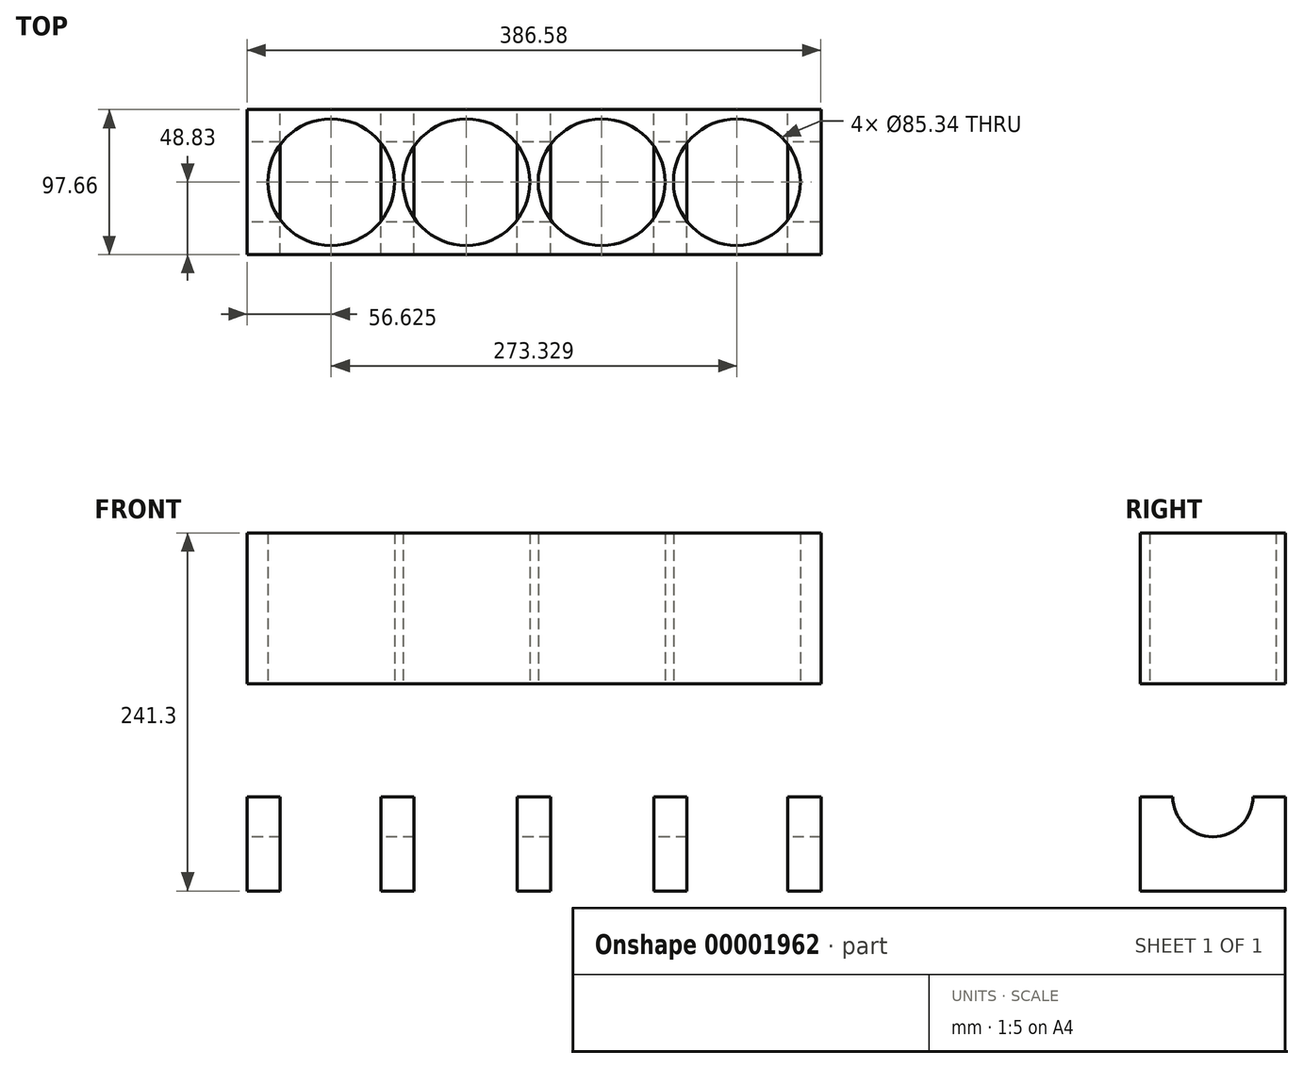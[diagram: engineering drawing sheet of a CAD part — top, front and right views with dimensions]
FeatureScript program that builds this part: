
annotation { "Feature Type Name" : "Feature", "Feature Type Description" : "" }
export const myFeature = defineFeature(function(context is Context, id is Id, definition is map)
    precondition{}
    {
        {
            var Q0;
            Q0=qCreatedBy(makeId("Front.planeOp"),FACE);
            var sketch = newSketch(context, id + "F0", { "sketchPlane" : qUnion([Q0])});
            skLineSegment(sketch, "E0.bottom", {"start": v(-193.3, 0) * mm, "end": v(-170.94, 0) * mm});
            skLineSegment(sketch, "E0.top", {"start": v(-193.3, -63.5) * mm, "end": v(-170.94, -63.5) * mm});
            skLineSegment(sketch, "E0.left", {"start": v(-193.3, 0) * mm, "end": v(-193.3, -63.5) * mm});
            skLineSegment(sketch, "E0.right", {"start": v(193.3, 0) * mm, "end": v(193.3, -63.5) * mm});
            skLineSegment(sketch, "E1", {"start": v(-170.94, 0) * mm, "end": v(-170.94, -63.5) * mm});
            skLineSegment(sketch, "E2", {"start": v(-103.05, 0) * mm, "end": v(-103.05, -63.5) * mm});
            skLineSegment(sketch, "E3", {"start": v(-80.7, 0) * mm, "end": v(-80.7, -63.5) * mm});
            skLineSegment(sketch, "E4", {"start": v(-11.18, 0) * mm, "end": v(-11.18, -63.5) * mm});
            skLineSegment(sketch, "E5", {"start": v(0, 0) * mm, "end": v(0, -63.5) * mm, "construction": true});
            skLineSegment(sketch, "E6.0.MirrorCS", {"start": v(11.18, 0) * mm, "end": v(11.18, -63.5) * mm});
            skLineSegment(sketch, "E7.0.MirrorCS", {"start": v(80.7, 0) * mm, "end": v(80.7, -63.5) * mm});
            skLineSegment(sketch, "E8.0.MirrorCS", {"start": v(103.05, 0) * mm, "end": v(103.05, -63.5) * mm});
            skLineSegment(sketch, "E9.0.MirrorCS", {"start": v(170.94, 0) * mm, "end": v(170.94, -63.5) * mm});
            skLineSegment(sketch, "E10.trimOffspring", {"start": v(-103.05, 0) * mm, "end": v(-80.7, 0) * mm});
            skLineSegment(sketch, "E11.trimOffspring", {"start": v(-103.05, -63.5) * mm, "end": v(-80.7, -63.5) * mm});
            skLineSegment(sketch, "E12.trimOffspring", {"start": v(-11.18, 0) * mm, "end": v(11.18, 0) * mm});
            skLineSegment(sketch, "E13.trimOffspring", {"start": v(-11.18, -63.5) * mm, "end": v(11.18, -63.5) * mm});
            skLineSegment(sketch, "E14.trimOffspring", {"start": v(80.7, 0) * mm, "end": v(103.05, 0) * mm});
            skLineSegment(sketch, "E15.trimOffspring", {"start": v(80.7, -63.5) * mm, "end": v(103.05, -63.5) * mm});
            skLineSegment(sketch, "E16.trimOffspring", {"start": v(170.94, 0) * mm, "end": v(193.3, 0) * mm});
            skLineSegment(sketch, "E17.trimOffspring", {"start": v(170.94, -63.5) * mm, "end": v(193.3, -63.5) * mm});
            skSolve(sketch);
        }
        {
            var Q0;
            {Q0=qUnion([makeQuery(id+"F0.imprint","IMPRINT",FACE,{"disambiguationData":[TD([[makeQuery(id+"F0.imprint","IMPRINT",EDGE,{"derivedFrom":sQuery(id+"F0.wireOp",EDGE,"E0.bottom")}),-1.0]])]}),makeQuery(id+"F0.imprint","IMPRINT",FACE,{"disambiguationData":[TD([[makeQuery(id+"F0.imprint","IMPRINT",EDGE,{"derivedFrom":sQuery(id+"F0.wireOp",EDGE,"E0.right")}),-1.0]])]}),makeQuery(id+"F0.imprint","IMPRINT",FACE,{"disambiguationData":[TD([[makeQuery(id+"F0.imprint","IMPRINT",EDGE,{"derivedFrom":sQuery(id+"F0.wireOp",EDGE,"E2")}),1.0]])]}),makeQuery(id+"F0.imprint","IMPRINT",FACE,{"disambiguationData":[TD([[makeQuery(id+"F0.imprint","IMPRINT",EDGE,{"derivedFrom":sQuery(id+"F0.wireOp",EDGE,"E4")}),1.0]])]}),makeQuery(id+"F0.imprint","IMPRINT",FACE,{"disambiguationData":[TD([[makeQuery(id+"F0.imprint","IMPRINT",EDGE,{"derivedFrom":sQuery(id+"F0.wireOp",EDGE,"E7.0.MirrorCS")}),1.0]])]})]);}
            extrude(context, id + "F1", {"entities" : qUnion([Q0]), "endBound" : BoundingType.SYMMETRIC, "depth" : 97.66 * mm});
        }
        {
            var Q0;
            Q0=makeQuery(id+"F1.opExtrude","SWEPT_FACE",FACE,{"disambiguationData":[OSD([sQuery(id+"F0.wireOp",EDGE,"E0.left")])]});
            var sketch = newSketch(context, id + "F2", { "sketchPlane" : qUnion([Q0])});
            skCircle(sketch, "E18", {"center": v(0, 0) * mm, "radius": 26.99 * mm});
            skSolve(sketch);
        }
        {
            var Q0;
            {var subQ0=makeQuery(id+"F1.opExtrude","SWEPT_EDGE",EDGE,{"disambiguationData":[OSD([sQuery(id+"F0.wireOp",EDGE,"E0.bottom"),sQuery(id+"F0.wireOp",EDGE,"E0.left")])]});var subQ1=sQuery(id+"F2.wireOp",EDGE,"E18");var subQ3=makeQuery(id+"F2.imprint","INTERSECT",VERTEX,{"disambiguationData":[OD(0.0)],"derivedFrom":[subQ0,subQ1]});Q0=qUnion([makeQuery(id+"F2.imprint","IMPRINT",FACE,{"disambiguationData":[TD([[makeQuery(id+"F2.imprint","IMPRINT",EDGE,{"disambiguationData":[TD([[subQ3,1.0]])],"derivedFrom":subQ1}),1.0]])]}),makeQuery(id+"F2.imprint","IMPRINT",FACE,{"disambiguationData":[TD([[makeQuery(id+"F2.imprint","IMPRINT",EDGE,{"disambiguationData":[TD([[subQ3,-1.0]])],"derivedFrom":subQ1}),1.0]])]})]);}
            extrude(context, id + "F3", {"entities" : qUnion([Q0]), "operationType" : NewBodyOperationType.REMOVE, "endBound" : BoundingType.THROUGH_ALL, "oppositeDirection" : true, "depth" : 25.4 * mm});
        }
        {
            var Q0;
            Q0=qCreatedBy(makeId("Top.planeOp"),FACE);
            cPlane(context, id + "F4", {"entities" : qUnion([Q0]), "cplaneType" : CPlaneType.OFFSET, "offset" : 76.2 * mm, "width" : 381 * mm, "height" : 381 * mm});
        }
        {
            var Q0;
            Q0=qCreatedBy(id+"F4.planeOp",FACE);
            var sketch = newSketch(context, id + "F5", { "sketchPlane" : qUnion([Q0])});
            skCircle(sketch, "E19", {"center": v(-45.55, 0) * mm, "radius": 42.67 * mm});
            skCircle(sketch, "E20", {"center": v(-136.66, 0) * mm, "radius": 42.67 * mm});
            skLineSegment(sketch, "E21", {"start": v(0, 48.83) * mm, "end": v(0, -48.83) * mm, "construction": true});
            skCircle(sketch, "E22.0.MirrorC", {"center": v(45.55, 0) * mm, "radius": 42.67 * mm});
            skCircle(sketch, "E23.0.MirrorC", {"center": v(136.66, 0) * mm, "radius": 42.67 * mm});
            skLineSegment(sketch, "E24.bottom", {"start": v(-193.3, 48.83) * mm, "end": v(193.3, 48.83) * mm});
            skLineSegment(sketch, "E24.top", {"start": v(-193.3, -48.83) * mm, "end": v(193.3, -48.83) * mm});
            skLineSegment(sketch, "E24.left", {"start": v(-193.3, 48.83) * mm, "end": v(-193.3, -48.83) * mm});
            skLineSegment(sketch, "E24.right", {"start": v(193.3, 48.83) * mm, "end": v(193.3, -48.83) * mm});
            skSolve(sketch);
        }
        {
            var Q0;
            Q0=makeQuery(id+"F5.imprint","IMPRINT",FACE,{"disambiguationData":[TD([[makeQuery(id+"F5.imprint","IMPRINT",EDGE,{"derivedFrom":sQuery(id+"F5.wireOp",EDGE,"E19")}),-1.0]])]});
            extrude(context, id + "F6", {"entities" : qUnion([Q0]), "depth" : 101.6 * mm});
        }
    });
